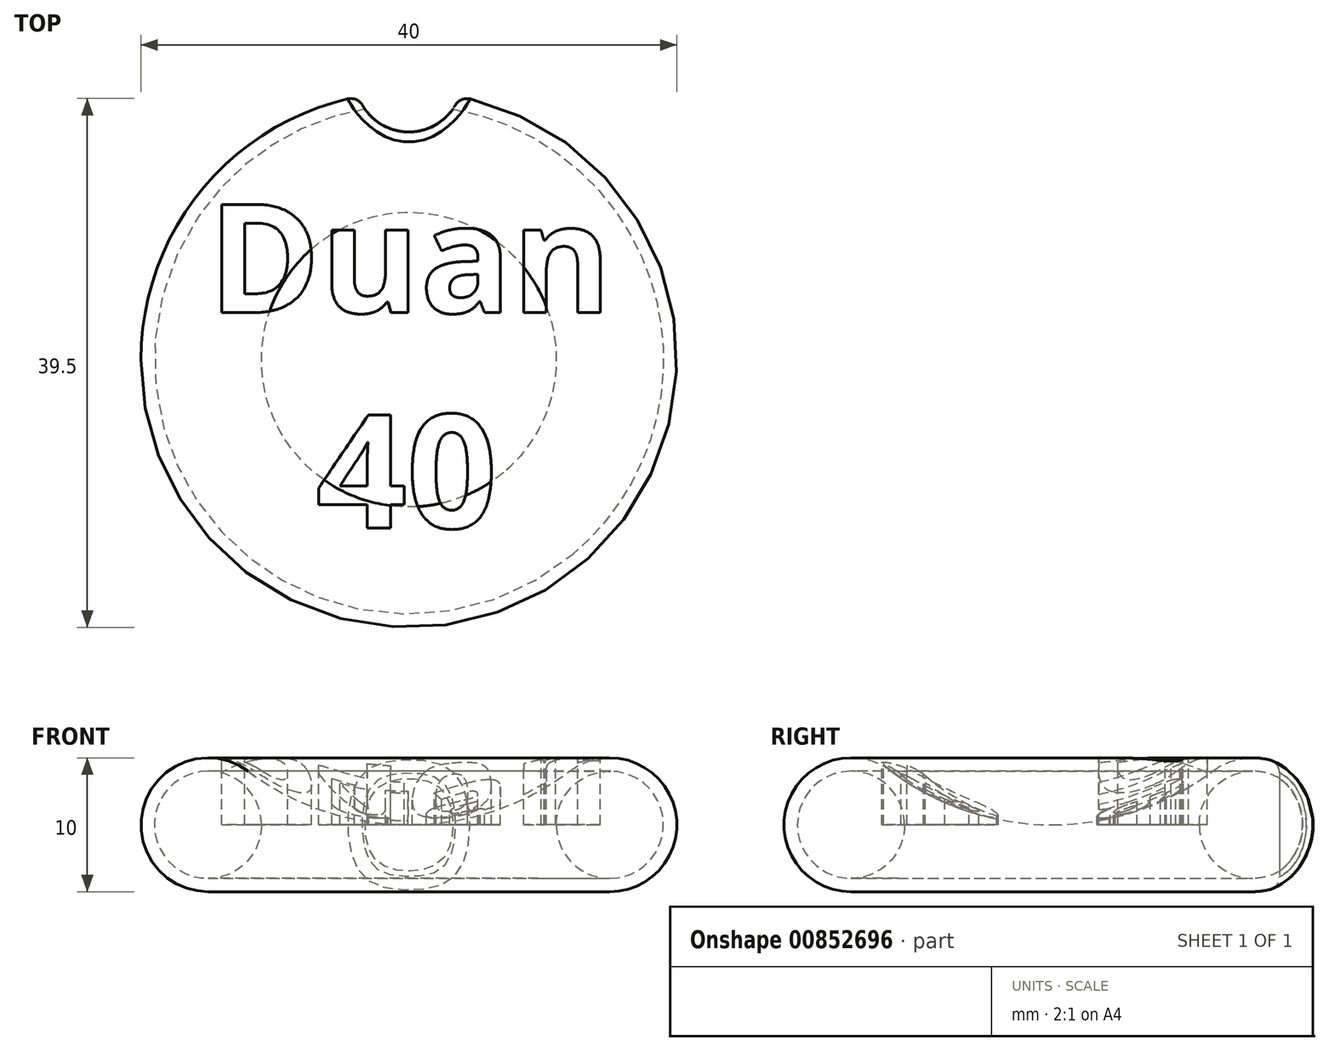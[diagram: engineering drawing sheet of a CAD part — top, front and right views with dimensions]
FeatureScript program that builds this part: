
annotation { "Feature Type Name" : "Feature", "Feature Type Description" : "" }
export const myFeature = defineFeature(function(context is Context, id is Id, definition is map)
    precondition{}
    {
        {
            var Q0;
            Q0=qCreatedBy(makeId("Front.planeOp"),FACE);
            var sketch = newSketch(context, id + "F0", { "sketchPlane" : qUnion([Q0])});
            skArc(sketch, "E0", {"start": v(-12, 9) * mm, "mid": v(-19.74, 6.58) * mm, "end": v(-15, 0) * mm});
            skArc(sketch, "E1", {"start": v(-12, 9) * mm, "mid": v(-6.32, 6.03) * mm, "end": v(0, 5) * mm});
            skLineSegment(sketch, "E2", {"start": v(-15, 0) * mm, "end": v(0, 0) * mm});
            skLineSegment(sketch, "E3", {"start": v(0, 0) * mm, "end": v(0, 5) * mm});
            skSolve(sketch);
        }
        {
            var Q0;
            Q0=makeQuery(id+"F0.imprint","IMPRINT",FACE,{"disambiguationData":[TD([[makeQuery(id+"F0.imprint","IMPRINT",EDGE,{"derivedFrom":sQuery(id+"F0.wireOp",EDGE,"E0")}),1.0]])]});
            var Q1;
            Q1=sQuery(id+"F0.wireOp",EDGE,"E3");
            revolve(context, id + "F1", {"surfaceOperationType" : NewSurfaceOperationType.NEW, "entities" : qUnion([Q0]), "axis" : qUnion([Q1]), "revolveType" : RevolveType.FULL});
        }
        {
            var Q0;
            Q0=qCreatedBy(makeId("Top.planeOp"),FACE);
            cPlane(context, id + "F2", {"entities" : qUnion([Q0]), "cplaneType" : CPlaneType.OFFSET, "offset" : 10 * mm, "width" : 150 * mm, "height" : 150 * mm});
        }
        {
            var Q0;
            Q0=qCreatedBy(id+"F2.planeOp",FACE);
            var sketch = newSketch(context, id + "F3", { "sketchPlane" : qUnion([Q0])});
            skText(sketch, "E4", { "text": "40", "fontName": "OpenSans-Bold.ttf"});
            skText(sketch, "E5", { "text": "Duan", "fontName": "OpenSans-Bold.ttf"});
            skLineSegment(sketch, "E6", {"start": v(0, 3.5) * mm, "end": v(0, -4.06) * mm, "construction": true});
            const initialGuessF3  = {"E4": [-0.00693, -0.01258, 1, 0, 0.00852], "E5": [-0.015, 0.0035, 1, 0, 0.00816]};
            skSetInitialGuess(sketch, initialGuessF3);
            skSolve(sketch);
        }
        {
            var Q0;
            Q0 = qSketchRegion(id + "F3", true);
            extrude(context, id + "F4", {"entities" : qUnion([Q0]), "operationType" : NewBodyOperationType.REMOVE, "oppositeDirection" : true, "depth" : 5 * mm, "offsetDistance" : 25 * mm});
        }
        {
            var Q0;
            Q0=qCreatedBy(makeId("Front.planeOp"),FACE);
            var sketch = newSketch(context, id + "F5", { "sketchPlane" : qUnion([Q0])});
            skCircle(sketch, "E7", {"center": v(-15, 5) * mm, "radius": 4 * mm});
            skSolve(sketch);
        }
        {
            var Q0;
            Q0 = qSketchRegion(id + "F5", true);
            var Q1;
            Q1=sQuery(id+"F0.wireOp",EDGE,"E3");
            revolve(context, id + "F6", {"surfaceOperationType" : NewSurfaceOperationType.NEW, "entities" : qUnion([Q0]), "axis" : qUnion([Q1]), "revolveType" : RevolveType.FULL});
        }
        {
            var Q0;
            Q0=qCreatedBy(makeId("Top.planeOp"),FACE);
            var sketch = newSketch(context, id + "F7", { "sketchPlane" : qUnion([Q0])});
            skCircle(sketch, "E8", {"center": v(0, 21) * mm, "radius": 4 * mm});
            skSolve(sketch);
        }
        {
            var Q0;
            Q0 = qSketchRegion(id + "F7", true);
            extrude(context, id + "F8", {"entities" : qUnion([Q0]), "operationType" : NewBodyOperationType.REMOVE, "depth" : 25 * mm, "offsetDistance" : 25 * mm});
        }
        {
            var Q0;
            Q0=makeQuery(id+"F8.boolean.opBoolean","INTERSECT",EDGE,{"derivedFrom":[makeQuery(id+"F4.boolean.opBoolean","SPLIT",FACE,{"disambiguationData":[TD([makeQuery(id+"F1.opRevolve","SWEPT_FACE",FACE,{"disambiguationData":[OSD([sQuery(id+"F0.wireOp",EDGE,"E1")])]}),makeQuery(id+"F1.opRevolve","SWEPT_FACE",FACE,{"disambiguationData":[OSD([sQuery(id+"F0.wireOp",EDGE,"E2")])]}),makeQuery(id+"F4.opExtrude","SWEPT_FACE",FACE,{"disambiguationData":[OSD([sQuery(id+"F3.wireOp",EDGE,"E4.sketch_text.stroke-1")])]}),makeQuery(id+"F4.opExtrude","SWEPT_FACE",FACE,{"disambiguationData":[OSD([sQuery(id+"F3.wireOp",EDGE,"E4.sketch_text.stroke-2")])]}),makeQuery(id+"F4.opExtrude","SWEPT_FACE",FACE,{"disambiguationData":[OSD([sQuery(id+"F3.wireOp",EDGE,"E4.sketch_text.stroke-3")])]}),makeQuery(id+"F4.opExtrude","SWEPT_FACE",FACE,{"disambiguationData":[OSD([sQuery(id+"F3.wireOp",EDGE,"E4.sketch_text.stroke-4")])]}),makeQuery(id+"F4.opExtrude","SWEPT_FACE",FACE,{"disambiguationData":[OSD([sQuery(id+"F3.wireOp",EDGE,"E4.sketch_text.stroke-5")])]}),makeQuery(id+"F4.opExtrude","SWEPT_FACE",FACE,{"disambiguationData":[OSD([sQuery(id+"F3.wireOp",EDGE,"E4.sketch_text.stroke-18")])]}),makeQuery(id+"F4.opExtrude","SWEPT_FACE",FACE,{"disambiguationData":[OSD([sQuery(id+"F3.wireOp",EDGE,"E4.sketch_text.stroke-19")])]}),makeQuery(id+"F4.opExtrude","SWEPT_FACE",FACE,{"disambiguationData":[OSD([sQuery(id+"F3.wireOp",EDGE,"E4.sketch_text.stroke-20")])]}),makeQuery(id+"F4.opExtrude","SWEPT_FACE",FACE,{"disambiguationData":[OSD([sQuery(id+"F3.wireOp",EDGE,"E5.sketch_text.stroke-1")])]}),makeQuery(id+"F4.opExtrude","SWEPT_FACE",FACE,{"disambiguationData":[OSD([sQuery(id+"F3.wireOp",EDGE,"E5.sketch_text.stroke-2")])]}),makeQuery(id+"F4.opExtrude","SWEPT_FACE",FACE,{"disambiguationData":[OSD([sQuery(id+"F3.wireOp",EDGE,"E5.sketch_text.stroke-3")])]}),makeQuery(id+"F4.opExtrude","SWEPT_FACE",FACE,{"disambiguationData":[OSD([sQuery(id+"F3.wireOp",EDGE,"E5.sketch_text.stroke-4")])]}),makeQuery(id+"F4.opExtrude","SWEPT_FACE",FACE,{"disambiguationData":[OSD([sQuery(id+"F3.wireOp",EDGE,"E5.sketch_text.stroke-5")])]}),makeQuery(id+"F4.opExtrude","SWEPT_FACE",FACE,{"disambiguationData":[OSD([sQuery(id+"F3.wireOp",EDGE,"E5.sketch_text.stroke-6")])]}),makeQuery(id+"F4.opExtrude","SWEPT_FACE",FACE,{"disambiguationData":[OSD([sQuery(id+"F3.wireOp",EDGE,"E5.sketch_text.stroke-54")])]}),makeQuery(id+"F4.opExtrude","SWEPT_FACE",FACE,{"disambiguationData":[OSD([sQuery(id+"F3.wireOp",EDGE,"E5.sketch_text.stroke-55")])]}),makeQuery(id+"F4.opExtrude","SWEPT_FACE",FACE,{"disambiguationData":[OSD([sQuery(id+"F3.wireOp",EDGE,"E5.sketch_text.stroke-56")])]}),makeQuery(id+"F4.opExtrude","SWEPT_FACE",FACE,{"disambiguationData":[OSD([sQuery(id+"F3.wireOp",EDGE,"E5.sketch_text.stroke-57")])]}),makeQuery(id+"F4.opExtrude","SWEPT_FACE",FACE,{"disambiguationData":[OSD([sQuery(id+"F3.wireOp",EDGE,"E5.sketch_text.stroke-58")])]}),makeQuery(id+"F4.opExtrude","SWEPT_FACE",FACE,{"disambiguationData":[OSD([sQuery(id+"F3.wireOp",EDGE,"E5.sketch_text.stroke-59")])]}),makeQuery(id+"F4.opExtrude","SWEPT_FACE",FACE,{"disambiguationData":[OSD([sQuery(id+"F3.wireOp",EDGE,"E5.sketch_text.stroke-60")])]}),makeQuery(id+"F4.opExtrude","SWEPT_FACE",FACE,{"disambiguationData":[OSD([sQuery(id+"F3.wireOp",EDGE,"E5.sketch_text.stroke-62")])]}),makeQuery(id+"F4.opExtrude","SWEPT_FACE",FACE,{"disambiguationData":[OSD([sQuery(id+"F3.wireOp",EDGE,"E5.sketch_text.stroke-63")])]}),makeQuery(id+"F4.opExtrude","SWEPT_FACE",FACE,{"disambiguationData":[OSD([sQuery(id+"F3.wireOp",EDGE,"E5.sketch_text.stroke-64")])]}),makeQuery(id+"F4.opExtrude","SWEPT_FACE",FACE,{"disambiguationData":[OSD([sQuery(id+"F3.wireOp",EDGE,"E5.sketch_text.stroke-65")])]}),makeQuery(id+"F4.opExtrude","SWEPT_FACE",FACE,{"disambiguationData":[OSD([sQuery(id+"F3.wireOp",EDGE,"E5.sketch_text.stroke-66")])]}),makeQuery(id+"F4.opExtrude","SWEPT_FACE",FACE,{"disambiguationData":[OSD([sQuery(id+"F3.wireOp",EDGE,"E5.sketch_text.stroke-67")])]}),makeQuery(id+"F4.opExtrude","SWEPT_FACE",FACE,{"disambiguationData":[OSD([sQuery(id+"F3.wireOp",EDGE,"E5.sketch_text.stroke-68")])]}),makeQuery(id+"F4.opExtrude","SWEPT_FACE",FACE,{"disambiguationData":[OSD([sQuery(id+"F3.wireOp",EDGE,"E5.sketch_text.stroke-69")])]}),makeQuery(id+"F4.opExtrude","SWEPT_FACE",FACE,{"disambiguationData":[OSD([sQuery(id+"F3.wireOp",EDGE,"E5.sketch_text.stroke-70")])]})])],"derivedFrom":makeQuery(id+"F1.opRevolve","SWEPT_FACE",FACE,{"disambiguationData":[OSD([sQuery(id+"F0.wireOp",EDGE,"E0")])]})}),makeQuery(id+"F8.opExtrude","SWEPT_FACE",FACE,{"disambiguationData":[OSD([sQuery(id+"F7.wireOp",EDGE,"E8")])]})]});
            fillet(context, id + "F9", {"entities" : qUnion([Q0]), "radius" : 1 * mm, "tangentPropagation" : true, "allowEdgeOverflow" : false});
        }
    });
